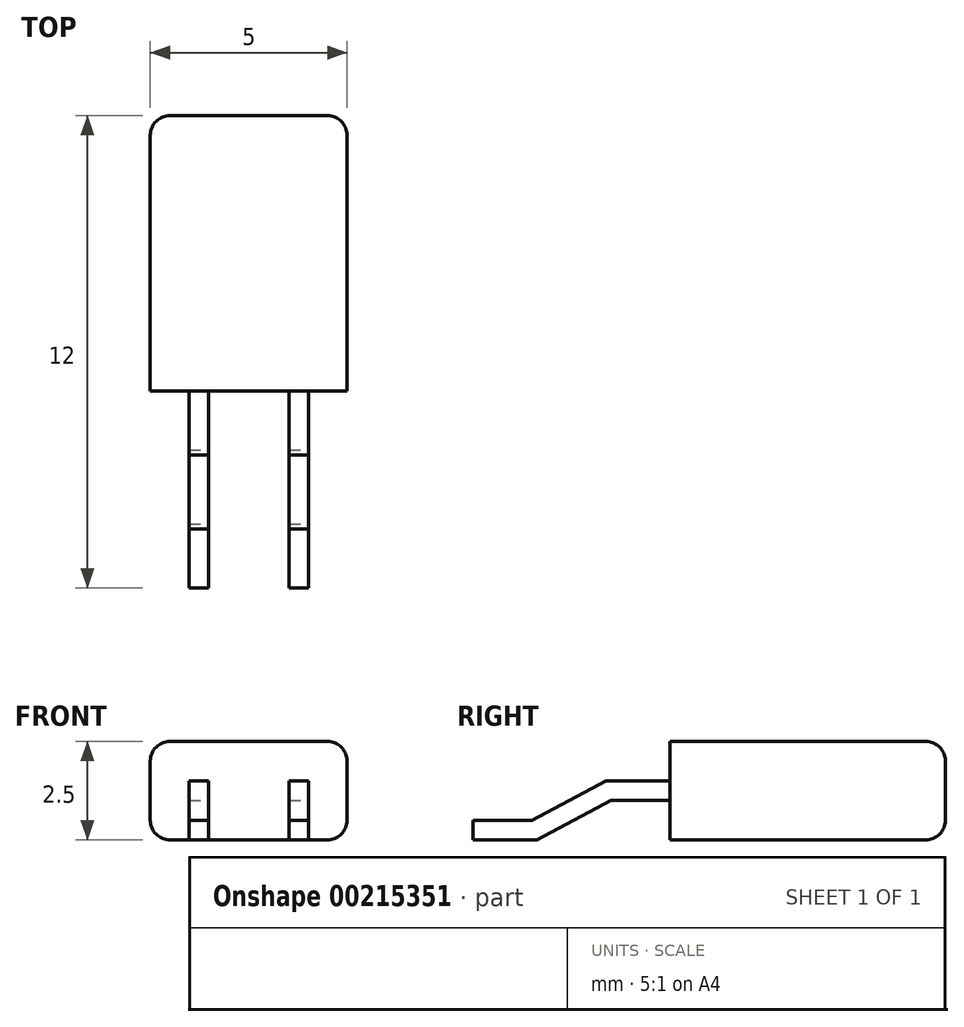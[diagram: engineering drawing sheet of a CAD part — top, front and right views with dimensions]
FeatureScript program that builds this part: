
annotation { "Feature Type Name" : "Feature", "Feature Type Description" : "" }
export const myFeature = defineFeature(function(context is Context, id is Id, definition is map)
    precondition{}
    {
        {
            var Q0;
            Q0=qCreatedBy(makeId("Top.planeOp"),FACE);
            var sketch = newSketch(context, id + "F0", { "sketchPlane" : qUnion([Q0])});
            skLineSegment(sketch, "E0.bottom", {"start": v(-2.5, 3.5) * mm, "end": v(2.5, 3.5) * mm});
            skLineSegment(sketch, "E0.top", {"start": v(-2.5, -3.5) * mm, "end": v(2.5, -3.5) * mm});
            skLineSegment(sketch, "E0.left", {"start": v(-2.5, 3.5) * mm, "end": v(-2.5, -3.5) * mm});
            skLineSegment(sketch, "E0.right", {"start": v(2.5, 3.5) * mm, "end": v(2.5, -3.5) * mm});
            skPoint(sketch, "E0.middle", {"position": v(0, 0) * mm});
            skSolve(sketch);
        }
        {
            var Q0;
            Q0 = qSketchRegion(id + "F0", true);
            extrude(context, id + "F1", {"entities" : qUnion([Q0]), "depth" : 2.5 * mm});
        }
        {
            var Q0;
            Q0=makeQuery(id+"F1.opExtrude","SWEPT_FACE",FACE,{"disambiguationData":[OSD([sQuery(id+"F0.wireOp",EDGE,"E0.top")])]});
            var sketch = newSketch(context, id + "F2", { "sketchPlane" : qUnion([Q0])});
            skLineSegment(sketch, "E1.top", {"start": v(-1.02, 1.5) * mm, "end": v(-1.52, 1.5) * mm});
            skLineSegment(sketch, "E1.left", {"start": v(-1.02, 1) * mm, "end": v(-1.02, 1.5) * mm});
            skLineSegment(sketch, "E1.right", {"start": v(-1.52, 1) * mm, "end": v(-1.52, 1.5) * mm});
            skPoint(sketch, "E1.middle", {"position": v(-1.27, 1.25) * mm});
            skLineSegment(sketch, "E2.top", {"start": v(1.52, 1.5) * mm, "end": v(1.02, 1.5) * mm});
            skLineSegment(sketch, "E2.left", {"start": v(1.52, 1) * mm, "end": v(1.52, 1.5) * mm});
            skLineSegment(sketch, "E2.right", {"start": v(1.02, 1) * mm, "end": v(1.02, 1.5) * mm});
            skPoint(sketch, "E2.middle", {"position": v(1.27, 1.25) * mm});
            skLineSegment(sketch, "E3.top", {"start": v(-1.52, 0) * mm, "end": v(-1.02, 0) * mm});
            skLineSegment(sketch, "E3.left", {"start": v(-1.52, 1) * mm, "end": v(-1.52, 0) * mm});
            skLineSegment(sketch, "E3.right", {"start": v(-1.02, 1) * mm, "end": v(-1.02, 0) * mm});
            skLineSegment(sketch, "E4.top", {"start": v(1.02, 0) * mm, "end": v(1.52, 0) * mm});
            skLineSegment(sketch, "E4.left", {"start": v(1.02, 1) * mm, "end": v(1.02, 0) * mm});
            skLineSegment(sketch, "E4.right", {"start": v(1.52, 1) * mm, "end": v(1.52, 0) * mm});
            skSolve(sketch);
        }
        {
            var Q0;
            Q0=makeQuery(id+"F1.opExtrude","CAP_EDGE",EDGE,{"disambiguationData":[OSD([sQuery(id+"F0.wireOp",EDGE,"E0.right")])],"isStart":false});
            var Q1;
            Q1=makeQuery(id+"F1.opExtrude","CAP_EDGE",EDGE,{"disambiguationData":[OSD([sQuery(id+"F0.wireOp",EDGE,"E0.right")])],"isStart":true});
            var Q2;
            Q2=makeQuery(id+"F1.opExtrude","CAP_EDGE",EDGE,{"disambiguationData":[OSD([sQuery(id+"F0.wireOp",EDGE,"E0.left")])],"isStart":true});
            var Q3;
            Q3=makeQuery(id+"F1.opExtrude","CAP_EDGE",EDGE,{"disambiguationData":[OSD([sQuery(id+"F0.wireOp",EDGE,"E0.left")])],"isStart":false});
            var Q4;
            Q4=makeQuery(id+"F1.opExtrude","CAP_EDGE",EDGE,{"disambiguationData":[OSD([sQuery(id+"F0.wireOp",EDGE,"E0.bottom")])],"isStart":true});
            var Q5;
            Q5=makeQuery(id+"F1.opExtrude","CAP_EDGE",EDGE,{"disambiguationData":[OSD([sQuery(id+"F0.wireOp",EDGE,"E0.bottom")])],"isStart":false});
            var Q6;
            Q6=makeQuery(id+"F1.opExtrude","SWEPT_EDGE",EDGE,{"disambiguationData":[OSD([sQuery(id+"F0.wireOp",EDGE,"E0.bottom"),sQuery(id+"F0.wireOp",EDGE,"E0.left")])]});
            var Q7;
            Q7=makeQuery(id+"F1.opExtrude","SWEPT_EDGE",EDGE,{"disambiguationData":[OSD([sQuery(id+"F0.wireOp",EDGE,"E0.bottom"),sQuery(id+"F0.wireOp",EDGE,"E0.right")])]});
            fillet(context, id + "F3", {"entities" : qUnion([Q0, Q1, Q2, Q3, Q4, Q5, Q6, Q7]), "radius" : 0.5 * mm, "tangentPropagation" : true, "allowEdgeOverflow" : false});
        }
        {
            var Q0;
            Q0 = qSketchRegion(id + "F2", true);
            extrude(context, id + "F4", {"entities" : qUnion([Q0]), "depth" : 5 * mm});
        }
        {
            var Q0;
            Q0=makeQuery(id+"F4.opExtrude","SWEPT_FACE",FACE,{"disambiguationData":[OSD([sQuery(id+"F2.wireOp",EDGE,"E2.left"),sQuery(id+"F2.wireOp",EDGE,"E4.right")])]});
            var sketch = newSketch(context, id + "F5", { "sketchPlane" : qUnion([Q0])});
            skLineSegment(sketch, "E5.bottom", {"start": v(-8.5, 1.5) * mm, "end": v(-5.13, 1.5) * mm});
            skLineSegment(sketch, "E5.top", {"start": v(-6.88, 0) * mm, "end": v(-3.5, 0) * mm});
            skLineSegment(sketch, "E5.left", {"start": v(-8.5, 1.5) * mm, "end": v(-8.5, 0.5) * mm});
            skLineSegment(sketch, "E5.right", {"start": v(-3.5, 1.5) * mm, "end": v(-3.5, 0) * mm});
            skLineSegment(sketch, "E6.left", {"start": v(-8.5, 1.5) * mm, "end": v(-8.5, 1) * mm});
            skLineSegment(sketch, "E7.top", {"start": v(-8.5, 0.5) * mm, "end": v(-7, 0.5) * mm});
            skLineSegment(sketch, "E7.right", {"start": v(-3.5, 0) * mm, "end": v(-3.5, 0.5) * mm});
            skLineSegment(sketch, "E8", {"start": v(-7, 0.5) * mm, "end": v(-6.06, 1) * mm});
            skLineSegment(sketch, "E9", {"start": v(-5.94, 0.5) * mm, "end": v(-5, 1) * mm});
            skLineSegment(sketch, "E10", {"start": v(-6.06, 1) * mm, "end": v(-5.13, 1.5) * mm});
            skLineSegment(sketch, "E11.trimOffspring", {"start": v(-5, 1) * mm, "end": v(-3.5, 1) * mm});
            skLineSegment(sketch, "E12", {"start": v(-5.94, 0.5) * mm, "end": v(-6.88, 0) * mm});
            skSolve(sketch);
        }
        {
            var Q0;
            Q0 = qSketchRegion(id + "F5", true);
            extrude(context, id + "F6", {"entities" : qUnion([Q0]), "operationType" : NewBodyOperationType.REMOVE, "endBound" : BoundingType.THROUGH_ALL, "oppositeDirection" : true, "depth" : 25 * mm});
        }
    });
